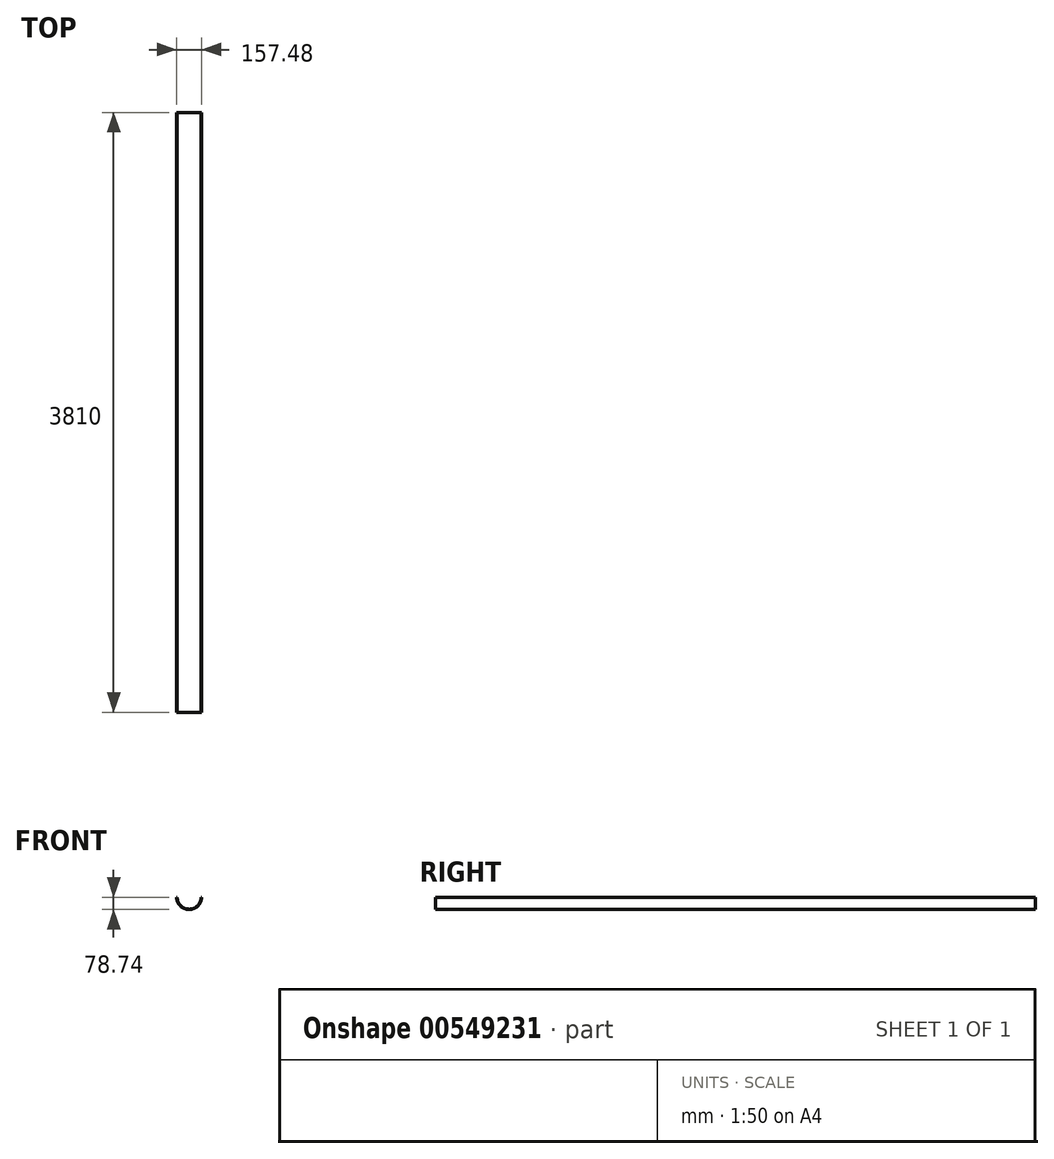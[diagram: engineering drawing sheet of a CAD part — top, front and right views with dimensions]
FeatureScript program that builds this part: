
annotation { "Feature Type Name" : "Feature", "Feature Type Description" : "" }
export const myFeature = defineFeature(function(context is Context, id is Id, definition is map)
    precondition{}
    {
        {
            var Q0;
            Q0=qCreatedBy(makeId("Front.planeOp"),FACE);
            var sketch = newSketch(context, id + "F0", { "sketchPlane" : qUnion([Q0])});
            skArc(sketch, "E0", {"start": v(-76.2, 0) * mm, "mid": v(0, -76.2) * mm, "end": v(76.2, 0) * mm});
            skArc(sketch, "E1", {"start": v(-78.74, 0) * mm, "mid": v(0, -78.74) * mm, "end": v(78.74, 0) * mm});
            skLineSegment(sketch, "E2", {"start": v(-78.74, 0) * mm, "end": v(-76.2, 0) * mm});
            skLineSegment(sketch, "E3.trimOffspring", {"start": v(76.2, 0) * mm, "end": v(78.74, 0) * mm});
            skSolve(sketch);
        }
        {
            var Q0;
            Q0 = qSketchRegion(id + "F0", true);
            extrude(context, id + "F1", {"entities" : qUnion([Q0]), "oppositeDirection" : true, "depth" : 3810 * mm, "offsetDistance" : 25.4 * mm});
        }
    });
